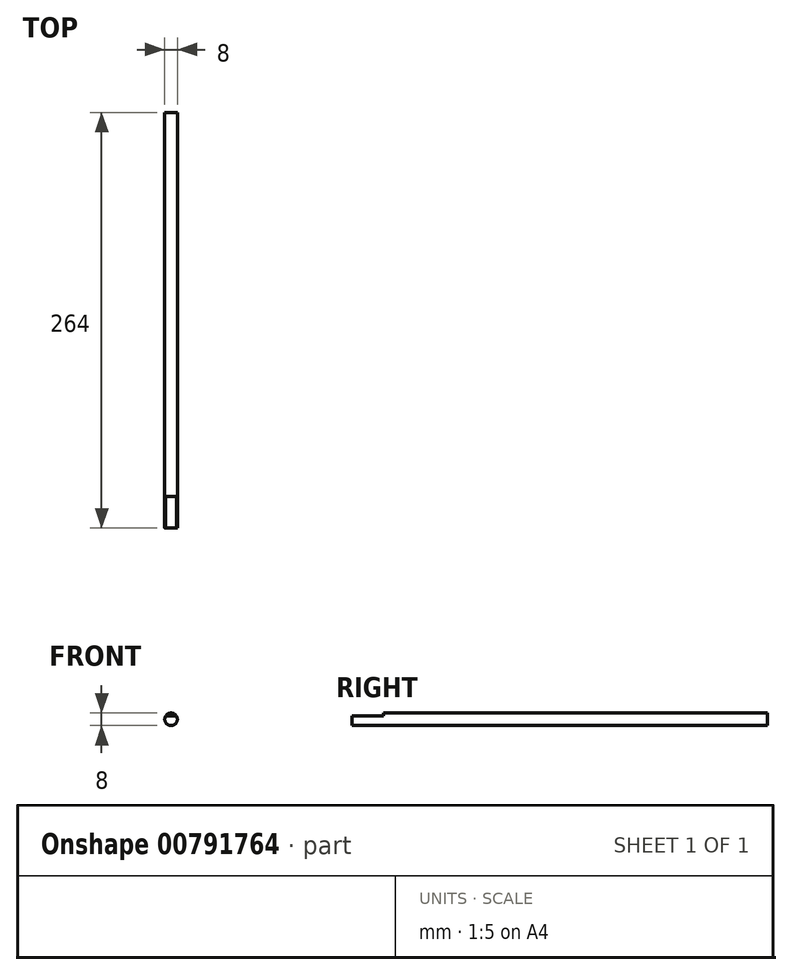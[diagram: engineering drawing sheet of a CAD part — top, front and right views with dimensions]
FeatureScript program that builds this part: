
annotation { "Feature Type Name" : "Feature", "Feature Type Description" : "" }
export const myFeature = defineFeature(function(context is Context, id is Id, definition is map)
    precondition{}
    {
        {
            var Q0;
            Q0=qCreatedBy(makeId("Front.planeOp"),FACE);
            var sketch = newSketch(context, id + "F0", { "sketchPlane" : qUnion([Q0])});
            skCircle(sketch, "E0", {"center": v(0, 0) * mm, "radius": 4 * mm});
            skSolve(sketch);
        }
        {
            var Q0;
            Q0 = qSketchRegion(id + "F0", true);
            extrude(context, id + "F1", {"entities" : qUnion([Q0]), "endBound" : BoundingType.SYMMETRIC, "depth" : 294 * mm, "offsetDistance" : 25 * mm});
        }
        {
            var Q0;
            Q0=makeQuery(id+"F1.opExtrude","CAP_FACE",FACE,{"disambiguationData":[OSD([sQuery(id+"F0.wireOp",EDGE,"E0")])],"isStart":false});
            var sketch = newSketch(context, id + "F2", { "sketchPlane" : qUnion([Q0])});
            skCircle(sketch, "E1.0", {"center": v(0, 0) * mm, "radius": 4 * mm});
            skLineSegment(sketch, "E2", {"start": v(-3.46, 2) * mm, "end": v(3.46, 2) * mm});
            skSolve(sketch);
        }
        {
            var Q0;
            {var subQ0=sQuery(id+"F2.wireOp",EDGE,"E2");Q0=makeQuery(id+"F2.imprint","IMPRINT",FACE,{"disambiguationData":[TD([[makeQuery(id+"F2.imprint","IMPRINT",EDGE,{"derivedFrom":subQ0}),1.0]])]});}
            extrude(context, id + "F3", {"entities" : qUnion([Q0]), "operationType" : NewBodyOperationType.REMOVE, "oppositeDirection" : true, "depth" : 20 * mm, "offsetDistance" : 25 * mm});
        }
        {
            var Q0;
            Q0=makeQuery(id+"F1.opExtrude","CAP_FACE",FACE,{"disambiguationData":[OSD([sQuery(id+"F0.wireOp",EDGE,"E0")])],"isStart":true});
            extrude(context, id + "F4", {"entities" : qUnion([Q0]), "operationType" : NewBodyOperationType.REMOVE, "oppositeDirection" : true, "depth" : 30 * mm, "offsetDistance" : 25 * mm});
        }
    });
